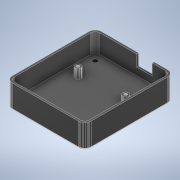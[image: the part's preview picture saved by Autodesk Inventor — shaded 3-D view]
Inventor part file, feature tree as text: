
AUTODESK INVENTOR PART (.ipt)
format: ipt  version: 2022 (Build 260153000, 153)  size: 975,872 bytes
history: native  units: mm
features: hole x4, sketch x4, other x3
ambient origin geometry x8: Origin, YZ Plane, XZ Plane, XY Plane, X Axis, Y Axis, Z Axis, Center Point
bodies: Body1 (feature_tree)
feature tree (11):
  other  "Sólido1"
  other  "nucleo-case-base"
  other  "MeshFeature1"
  hole  "Agujero1"  [1 undecoded]
  hole  "Agujero2"  [1 undecoded]
  hole  "Agujero3"  [1 undecoded]
  hole  "Agujero4"  [1 undecoded]
  sketch  "Boceto1"  dims[d0=10.0mm d1=10.0mm]
  sketch  "Boceto2"  dims[d2=5.0mm d3=6.0mm d4=4.0mm d5=2.0mm d6=90.0deg d7=8.0mm d8=20.594885mm d9=10.0mm]
  sketch  "Boceto3"  dims[d10=10.0mm]
  sketch  "Boceto4"  dims[d11=5.0mm d12=6.0mm d13=4.0mm d14=2.0mm d15=90.0deg d16=8.0mm d17=20.594885mm d18=10.0mm d19=10.0mm d20=5.0mm d21=6.0mm d22=4.0mm d23=2.0mm d24=90.0deg d25=8.0mm d26=20.594885mm d27=10.0mm d28=10.0mm d29=5.0mm d30=6.0mm d31=4.0mm d32=2.0mm d33=90.0deg d34=8.0mm d35=20.594885mm]
note: 4 required parameter values undecoded (feature->parameter linkage not recoverable at this tier; creation-order binding heuristic only, values carry confidence <= 0.55)
